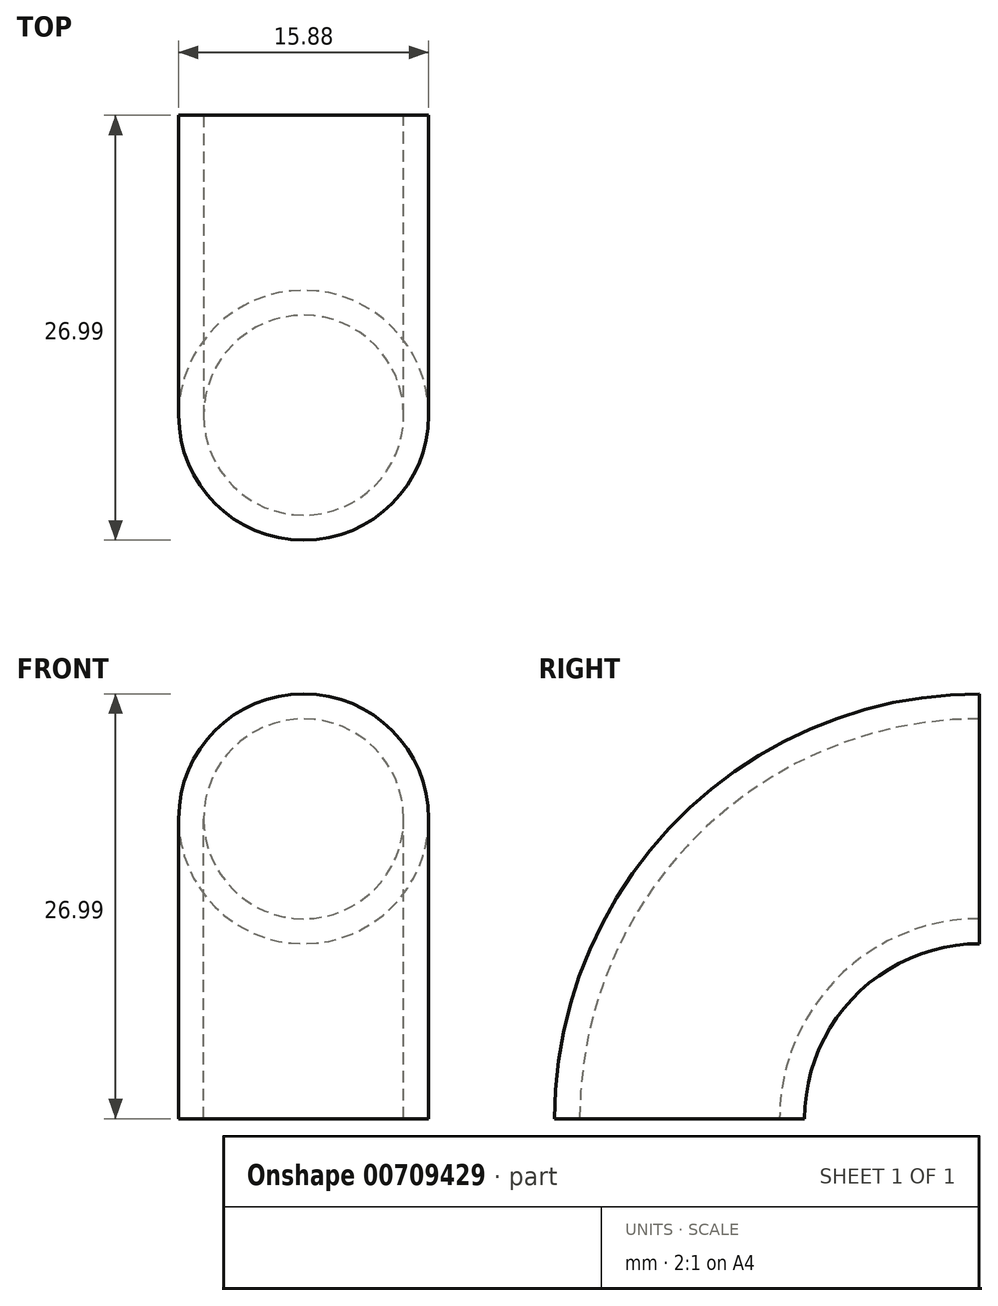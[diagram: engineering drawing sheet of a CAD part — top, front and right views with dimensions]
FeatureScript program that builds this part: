
annotation { "Feature Type Name" : "Feature", "Feature Type Description" : "" }
export const myFeature = defineFeature(function(context is Context, id is Id, definition is map)
    precondition{}
    {
        {
            var Q0;
            Q0=qCreatedBy(makeId("Top.planeOp"),FACE);
            var sketch = newSketch(context, id + "F0", { "sketchPlane" : qUnion([Q0])});
            skLineSegment(sketch, "E0", {"start": v(0, 0) * mm, "end": v(6.35, 0) * mm});
            skCircle(sketch, "E1", {"center": v(0, 0) * mm, "radius": 6.35 * mm});
            skCircle(sketch, "E2.0", {"center": v(0, 0) * mm, "radius": 7.94 * mm});
            skSolve(sketch);
        }
        {
            var Q0;
            Q0=qCreatedBy(makeId("Right.planeOp"),FACE);
            var sketch = newSketch(context, id + "F1", { "sketchPlane" : qUnion([Q0])});
            skLineSegment(sketch, "E3", {"start": v(0, 0) * mm, "end": v(0, 0) * mm});
            skLineSegment(sketch, "E4", {"start": v(0, 0) * mm, "end": v(19.05, 0) * mm});
            skArc(sketch, "E5", {"start": v(0, 0) * mm, "mid": v(5.58, 13.47) * mm, "end": v(19.05, 19.05) * mm});
            skSolve(sketch);
        }
        {
            var Q0;
            Q0=qSketchRegion(id+"F0",true);
            var Q1;
            Q1=sQuery(id+"F1.wireOp",EDGE,"E5");
            sweep(context, id + "F2", {"profiles" : qUnion([Q0]), "path" : qUnion([Q1])});
        }
    });
